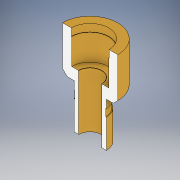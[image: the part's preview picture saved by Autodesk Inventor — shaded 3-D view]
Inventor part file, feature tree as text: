
AUTODESK INVENTOR PART (.ipt)
format: ipt  version: 2018 (Build 220112000, 112)  size: 167,936 bytes
history: native  units: in
note: dims shown in document units (in); Inventor stores cm internally (conversion verified against a paired STEP export)
features: sketch x7, extrude x4, hole x2, revolve x1, chamfer x1
ambient origin geometry x8: Origin, YZ Plane, XZ Plane, XY Plane, X Axis, Y Axis, Z Axis, Center Point
bodies: Solid1 (feature_tree)
feature tree (15):
  extrude  "Extrusion1"  Depth=1.2in TaperAngle=0.0deg
  hole  "Hole1"  [1 undecoded]
  hole  "Hole2"  [1 undecoded]
  extrude  "Extrusion3"  Depth=0.1in
  extrude  "Extrusion4"  Depth=0.6in
  extrude  "Extrusion5"  Depth=0.1in
  revolve  "Revolution1"  Angle=90.0deg
  chamfer  "Chamfer2"  Distance=0.01in
  sketch  "Sketch1"  dims[d0=0.75in d1=1.2in d2=0.0in]
  sketch  "Sketch3"  dims[d6=0.3125in d7=0.75in d8=0.375in d9=0.25in d10=0.5635in d11=1.0in d12=0.8108in]
  sketch  "Sketch4"  dims[d13=0.4844in d14=0.75in d15=0.375in d16=0.25in d17=0.5635in d18=0.4in d19=0.8108in d20=0.501in]
  sketch  "Sketch5"  dims[d21=0.45in d22=0.0in d23=0.51in]
  sketch  "Sketch6"  dims[d24=0.1in d25=0.0in d26=0.439in]
  sketch  "Sketch7"  dims[d27=0.6in d28=0.0in d35=0.44in]
  sketch  "Sketch9"  dims[d36=90.0deg d37=0.215in d38=90.0deg d39=0.01in d40=0.1in d41=90.0deg d42=0.0625in d43=0.125in d44=45.0deg d45=1.0in d46=1.0in]
note: 2 required parameter values undecoded (feature->parameter linkage not recoverable at this tier; creation-order binding heuristic only, values carry confidence <= 0.55)
